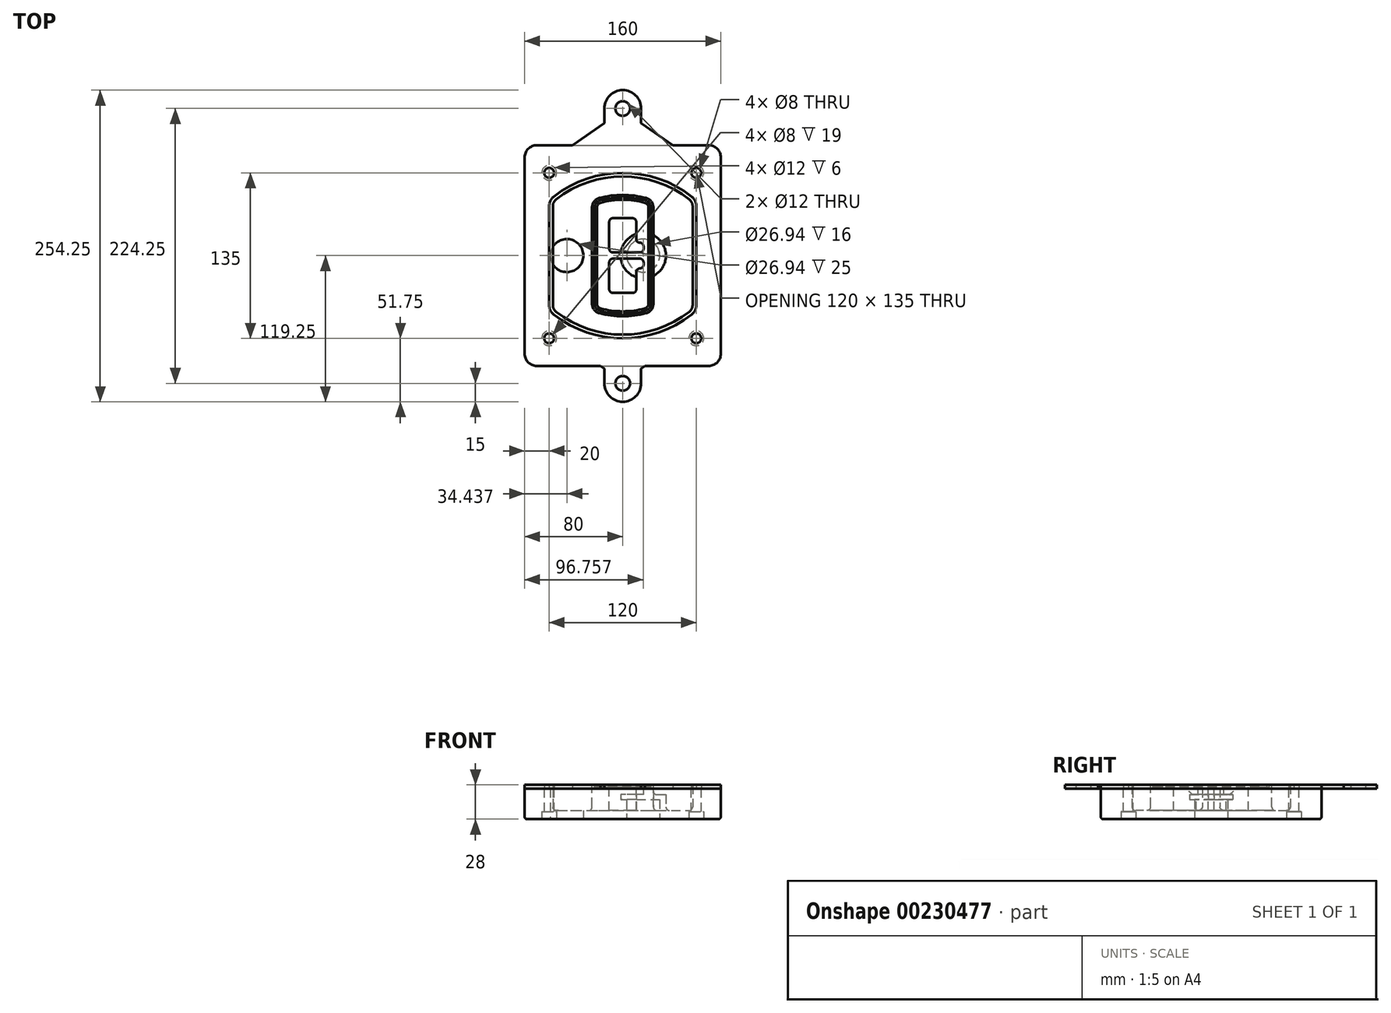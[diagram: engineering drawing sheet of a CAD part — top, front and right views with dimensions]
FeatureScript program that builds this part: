
annotation { "Feature Type Name" : "Feature", "Feature Type Description" : "" }
export const myFeature = defineFeature(function(context is Context, id is Id, definition is map)
    precondition{}
    {
        {
            var Q0;
            Q0=qCreatedBy(makeId("Top.planeOp"),FACE);
            var sketch = newSketch(context, id + "F0", { "sketchPlane" : qUnion([Q0])});
            skPoint(sketch, "E0.rect.middle", {"position": v(0, 0) * mm});
            skLineSegment(sketch, "E1.bottom", {"start": v(-70, -90) * mm, "end": v(70, -90) * mm});
            skLineSegment(sketch, "E1.top", {"start": v(-70, 90) * mm, "end": v(70, 90) * mm});
            skLineSegment(sketch, "E1.left", {"start": v(-80, -80) * mm, "end": v(-80, 80) * mm});
            skLineSegment(sketch, "E1.right", {"start": v(80, -80) * mm, "end": v(80, 80) * mm});
            skLineSegment(sketch, "E2", {"start": v(-80, 90) * mm, "end": v(80, -90) * mm, "construction": true});
            skLineSegment(sketch, "E3", {"start": v(80, 90) * mm, "end": v(-80, -90) * mm, "construction": true});
            skCircle(sketch, "E4", {"center": v(-60, 67.5) * mm, "radius": 4 * mm});
            skCircle(sketch, "E5", {"center": v(60, 67.5) * mm, "radius": 4 * mm});
            skCircle(sketch, "E6", {"center": v(60, -67.5) * mm, "radius": 4 * mm});
            skCircle(sketch, "E7", {"center": v(-60, -67.5) * mm, "radius": 4 * mm});
            skLineSegment(sketch, "E8", {"start": v(-60, 67.5) * mm, "end": v(60, 67.5) * mm, "construction": true});
            skLineSegment(sketch, "E9", {"start": v(60, 67.5) * mm, "end": v(60, -67.5) * mm, "construction": true});
            skLineSegment(sketch, "E10", {"start": v(60, -67.5) * mm, "end": v(-60, -67.5) * mm, "construction": true});
            skLineSegment(sketch, "E11", {"start": v(-60, -67.5) * mm, "end": v(-60, 67.5) * mm, "construction": true});
            skLineSegment(sketch, "E12", {"start": v(-60, 40.3) * mm, "end": v(-60, -40.3) * mm});
            skLineSegment(sketch, "E13", {"start": v(60, 40.3) * mm, "end": v(60, -40.3) * mm});
            skArc(sketch, "E14", {"start": v(56.15, 48.18) * mm, "mid": v(0, 67.5) * mm, "end": v(-56.15, 48.18) * mm});
            skArc(sketch, "E15", {"start": v(-56.15, -48.18) * mm, "mid": v(0, -67.5) * mm, "end": v(56.15, -48.18) * mm});
            skLineSegment(sketch, "E16", {"start": v(-60, 0) * mm, "end": v(60, 0) * mm, "construction": true});
            skPoint(sketch, "E17.visualSharp", {"position": v(-60, -45) * mm});
            skArc(sketch, "E17.filletArc", {"start": v(-60, -40.3) * mm, "mid": v(-58.99, -44.68) * mm, "end": v(-56.15, -48.18) * mm});
            skPoint(sketch, "E18.visualSharp", {"position": v(-60, 45) * mm});
            skArc(sketch, "E18.filletArc", {"start": v(-56.15, 48.18) * mm, "mid": v(-58.99, 44.68) * mm, "end": v(-60, 40.3) * mm});
            skPoint(sketch, "E19.visualSharp", {"position": v(60, 45) * mm});
            skArc(sketch, "E19.filletArc", {"start": v(60, 40.3) * mm, "mid": v(58.99, 44.68) * mm, "end": v(56.15, 48.18) * mm});
            skPoint(sketch, "E20.visualSharp", {"position": v(60, -45) * mm});
            skArc(sketch, "E20.filletArc", {"start": v(56.15, -48.18) * mm, "mid": v(58.99, -44.68) * mm, "end": v(60, -40.3) * mm});
            skPoint(sketch, "E21.visualSharp", {"position": v(-80, 90) * mm});
            skArc(sketch, "E21.filletArc", {"start": v(-70, 90) * mm, "mid": v(-77.07, 87.07) * mm, "end": v(-80, 80) * mm});
            skPoint(sketch, "E22.visualSharp", {"position": v(80, 90) * mm});
            skArc(sketch, "E22.filletArc", {"start": v(80, 80) * mm, "mid": v(77.07, 87.07) * mm, "end": v(70, 90) * mm});
            skPoint(sketch, "E23.visualSharp", {"position": v(80, -90) * mm});
            skArc(sketch, "E23.filletArc", {"start": v(70, -90) * mm, "mid": v(77.07, -87.07) * mm, "end": v(80, -80) * mm});
            skPoint(sketch, "E24.visualSharp", {"position": v(-80, -90) * mm});
            skArc(sketch, "E24.filletArc", {"start": v(-80, -80) * mm, "mid": v(-77.07, -87.07) * mm, "end": v(-70, -90) * mm});
            skArc(sketch, "E25.0", {"start": v(57, 40.3) * mm, "mid": v(56.3, 43.36) * mm, "end": v(54.3, 45.81) * mm});
            skLineSegment(sketch, "E25.1", {"start": v(57, 40.3) * mm, "end": v(57, -40.3) * mm});
            skArc(sketch, "E25.2", {"start": v(54.3, -45.81) * mm, "mid": v(56.3, -43.36) * mm, "end": v(57, -40.3) * mm});
            skArc(sketch, "E25.3", {"start": v(-54.3, -45.81) * mm, "mid": v(0, -64.5) * mm, "end": v(54.3, -45.81) * mm});
            skArc(sketch, "E25.4", {"start": v(-57, -40.3) * mm, "mid": v(-56.3, -43.36) * mm, "end": v(-54.3, -45.81) * mm});
            skArc(sketch, "E25.5", {"start": v(54.3, 45.81) * mm, "mid": v(0, 64.5) * mm, "end": v(-54.3, 45.81) * mm});
            skLineSegment(sketch, "E25.6", {"start": v(-57, 40.3) * mm, "end": v(-57, -40.3) * mm});
            skArc(sketch, "E25.7", {"start": v(-54.3, 45.81) * mm, "mid": v(-56.3, 43.36) * mm, "end": v(-57, 40.3) * mm});
            skArc(sketch, "E26.0", {"start": v(-58.62, 51.33) * mm, "mid": v(-62.58, 46.43) * mm, "end": v(-64, 40.3) * mm});
            skArc(sketch, "E26.1", {"start": v(58.62, 51.33) * mm, "mid": v(0, 71.5) * mm, "end": v(-58.62, 51.33) * mm});
            skArc(sketch, "E26.2", {"start": v(64, 40.3) * mm, "mid": v(62.58, 46.43) * mm, "end": v(58.62, 51.33) * mm});
            skLineSegment(sketch, "E26.3", {"start": v(64, 40.3) * mm, "end": v(64, -40.3) * mm});
            skArc(sketch, "E26.4", {"start": v(58.62, -51.33) * mm, "mid": v(62.58, -46.43) * mm, "end": v(64, -40.3) * mm});
            skLineSegment(sketch, "E26.5", {"start": v(-64, 40.3) * mm, "end": v(-64, -40.3) * mm});
            skArc(sketch, "E26.6", {"start": v(-58.62, -51.33) * mm, "mid": v(0, -71.5) * mm, "end": v(58.62, -51.33) * mm});
            skArc(sketch, "E26.7", {"start": v(-64, -40.3) * mm, "mid": v(-62.58, -46.43) * mm, "end": v(-58.62, -51.33) * mm});
            skSolve(sketch);
        }
        {
            var Q0;
            Q0=makeQuery(id+"F0.imprint","IMPRINT",FACE,{"disambiguationData":[TD([[makeQuery(id+"F0.imprint","IMPRINT",EDGE,{"derivedFrom":sQuery(id+"F0.wireOp",EDGE,"E1.bottom")}),1.0]])]});
            var Q1;
            Q1=makeQuery(id+"F0.imprint","IMPRINT",FACE,{"disambiguationData":[TD([[makeQuery(id+"F0.imprint","IMPRINT",EDGE,{"derivedFrom":sQuery(id+"F0.wireOp",EDGE,"E12")}),1.0]])]});
            var Q2;
            Q2=makeQuery(id+"F0.imprint","IMPRINT",FACE,{"disambiguationData":[TD([[makeQuery(id+"F0.imprint","IMPRINT",EDGE,{"derivedFrom":sQuery(id+"F0.wireOp",EDGE,"E25.0")}),1.0]])]});
            var Q3;
            Q3=makeQuery(id+"F0.imprint","IMPRINT",FACE,{"disambiguationData":[TD([[makeQuery(id+"F0.imprint","IMPRINT",EDGE,{"derivedFrom":sQuery(id+"F0.wireOp",EDGE,"E12")}),-1.0]])]});
            extrude(context, id + "F1", {"entities" : qUnion([Q0, Q1, Q2, Q3]), "oppositeDirection" : true, "depth" : 25 * mm});
        }
        {
            var Q0;
            Q0=makeQuery(id+"F0.imprint","IMPRINT",FACE,{"disambiguationData":[TD([[makeQuery(id+"F0.imprint","IMPRINT",EDGE,{"derivedFrom":sQuery(id+"F0.wireOp",EDGE,"E12")}),1.0]])]});
            extrude(context, id + "F2", {"entities" : qUnion([Q0]), "operationType" : NewBodyOperationType.ADD, "depth" : 3 * mm});
        }
        {
            var Q0;
            Q0=makeQuery(id+"F0.imprint","IMPRINT",FACE,{"disambiguationData":[TD([[makeQuery(id+"F0.imprint","IMPRINT",EDGE,{"derivedFrom":sQuery(id+"F0.wireOp",EDGE,"E25.0")}),1.0]])]});
            extrude(context, id + "F3", {"entities" : qUnion([Q0]), "operationType" : NewBodyOperationType.REMOVE, "oppositeDirection" : true, "depth" : 18 * mm});
        }
        {
            var Q0;
            Q0=makeQuery(id+"F2.opExtrude","CAP_FACE",FACE,{"disambiguationData":[OSD([sQuery(id+"F0.wireOp",EDGE,"E12"),sQuery(id+"F0.wireOp",EDGE,"E13"),sQuery(id+"F0.wireOp",EDGE,"E14"),sQuery(id+"F0.wireOp",EDGE,"E15"),sQuery(id+"F0.wireOp",EDGE,"E17.filletArc"),sQuery(id+"F0.wireOp",EDGE,"E18.filletArc"),sQuery(id+"F0.wireOp",EDGE,"E19.filletArc"),sQuery(id+"F0.wireOp",EDGE,"E20.filletArc"),sQuery(id+"F0.wireOp",EDGE,"E25.0"),sQuery(id+"F0.wireOp",EDGE,"E25.1"),sQuery(id+"F0.wireOp",EDGE,"E25.2"),sQuery(id+"F0.wireOp",EDGE,"E25.3"),sQuery(id+"F0.wireOp",EDGE,"E25.4"),sQuery(id+"F0.wireOp",EDGE,"E25.5"),sQuery(id+"F0.wireOp",EDGE,"E25.6"),sQuery(id+"F0.wireOp",EDGE,"E25.7")])],"isStart":false});
            var sketch = newSketch(context, id + "F4", { "sketchPlane" : qUnion([Q0])});
            skArc(sketch, "E27.0", {"start": v(-19.08, -46.97) * mm, "mid": v(0, -49.5) * mm, "end": v(19.08, -46.97) * mm});
            skArc(sketch, "E28.0", {"start": v(19.08, 46.97) * mm, "mid": v(0, 49.5) * mm, "end": v(-19.08, 46.97) * mm});
            skLineSegment(sketch, "E29", {"start": v(-25, 39.25) * mm, "end": v(-25, -39.25) * mm});
            skLineSegment(sketch, "E30", {"start": v(25, 39.25) * mm, "end": v(25, -39.25) * mm});
            skLineSegment(sketch, "E31", {"start": v(-25, 45.1) * mm, "end": v(25, 45.1) * mm, "construction": true});
            skLineSegment(sketch, "E32", {"start": v(-25, -45.1) * mm, "end": v(25, -45.1) * mm, "construction": true});
            skPoint(sketch, "E33.visualSharp", {"position": v(-25, 45.1) * mm});
            skArc(sketch, "E33.filletArc", {"start": v(-19.08, 46.97) * mm, "mid": v(-23.35, 44.11) * mm, "end": v(-25, 39.25) * mm});
            skPoint(sketch, "E34.visualSharp", {"position": v(25, 45.1) * mm});
            skArc(sketch, "E34.filletArc", {"start": v(25, 39.25) * mm, "mid": v(23.35, 44.11) * mm, "end": v(19.08, 46.97) * mm});
            skPoint(sketch, "E35.visualSharp", {"position": v(25, -45.1) * mm});
            skArc(sketch, "E35.filletArc", {"start": v(19.08, -46.97) * mm, "mid": v(23.35, -44.11) * mm, "end": v(25, -39.25) * mm});
            skPoint(sketch, "E36.visualSharp", {"position": v(-25, -45.1) * mm});
            skArc(sketch, "E36.filletArc", {"start": v(-25, -39.25) * mm, "mid": v(-23.35, -44.11) * mm, "end": v(-19.08, -46.97) * mm});
            skArc(sketch, "E37.0", {"start": v(54.3, 45.81) * mm, "mid": v(0, 64.5) * mm, "end": v(-54.3, 45.81) * mm});
            skArc(sketch, "E37.1", {"start": v(-54.3, 45.81) * mm, "mid": v(-56.3, 43.36) * mm, "end": v(-57, 40.3) * mm});
            skLineSegment(sketch, "E37.2", {"start": v(-57, 40.3) * mm, "end": v(-57, -40.3) * mm});
            skArc(sketch, "E37.3", {"start": v(-57, -40.3) * mm, "mid": v(-56.3, -43.36) * mm, "end": v(-54.3, -45.81) * mm});
            skArc(sketch, "E37.4", {"start": v(-54.3, -45.81) * mm, "mid": v(0, -64.5) * mm, "end": v(54.3, -45.81) * mm});
            skArc(sketch, "E37.5", {"start": v(54.3, -45.81) * mm, "mid": v(56.3, -43.36) * mm, "end": v(57, -40.3) * mm});
            skLineSegment(sketch, "E37.6", {"start": v(57, 40.3) * mm, "end": v(57, -40.3) * mm});
            skArc(sketch, "E37.7", {"start": v(57, 40.3) * mm, "mid": v(56.3, 43.36) * mm, "end": v(54.3, 45.81) * mm});
            skLineSegment(sketch, "E38.0", {"start": v(23, 39.25) * mm, "end": v(23, -39.25) * mm});
            skArc(sketch, "E38.1", {"start": v(18.56, -45.04) * mm, "mid": v(21.76, -42.9) * mm, "end": v(23, -39.25) * mm});
            skArc(sketch, "E38.2", {"start": v(-18.56, -45.04) * mm, "mid": v(0, -47.5) * mm, "end": v(18.56, -45.04) * mm});
            skArc(sketch, "E38.3", {"start": v(-23, -39.25) * mm, "mid": v(-21.76, -42.9) * mm, "end": v(-18.56, -45.04) * mm});
            skLineSegment(sketch, "E38.4", {"start": v(-23, 39.25) * mm, "end": v(-23, -39.25) * mm});
            skArc(sketch, "E38.5", {"start": v(23, 39.25) * mm, "mid": v(21.76, 42.9) * mm, "end": v(18.56, 45.04) * mm});
            skArc(sketch, "E38.6", {"start": v(-18.56, 45.04) * mm, "mid": v(-21.76, 42.9) * mm, "end": v(-23, 39.25) * mm});
            skArc(sketch, "E38.7", {"start": v(18.56, 45.04) * mm, "mid": v(0, 47.5) * mm, "end": v(-18.56, 45.04) * mm});
            skArc(sketch, "E39.0", {"start": v(21, 39.25) * mm, "mid": v(20.18, 41.68) * mm, "end": v(18.04, 43.1) * mm});
            skLineSegment(sketch, "E39.1", {"start": v(21, 39.25) * mm, "end": v(21, -39.25) * mm});
            skArc(sketch, "E39.2", {"start": v(18.04, -43.1) * mm, "mid": v(20.18, -41.68) * mm, "end": v(21, -39.25) * mm});
            skArc(sketch, "E39.3", {"start": v(-18.04, -43.1) * mm, "mid": v(0, -45.5) * mm, "end": v(18.04, -43.1) * mm});
            skArc(sketch, "E39.4", {"start": v(-21, -39.25) * mm, "mid": v(-20.18, -41.68) * mm, "end": v(-18.04, -43.1) * mm});
            skArc(sketch, "E39.5", {"start": v(18.04, 43.1) * mm, "mid": v(0, 45.5) * mm, "end": v(-18.04, 43.1) * mm});
            skLineSegment(sketch, "E39.6", {"start": v(-21, 39.25) * mm, "end": v(-21, -39.25) * mm});
            skArc(sketch, "E39.7", {"start": v(-18.04, 43.1) * mm, "mid": v(-20.18, 41.68) * mm, "end": v(-21, 39.25) * mm});
            skLineSegment(sketch, "E40", {"start": v(-25, 0) * mm, "end": v(25, 0) * mm, "construction": true});
            skLineSegment(sketch, "E41", {"start": v(-11, 5.5) * mm, "end": v(-11, 27.5) * mm});
            skLineSegment(sketch, "E42", {"start": v(-8, 30.5) * mm, "end": v(8, 30.5) * mm});
            skLineSegment(sketch, "E43", {"start": v(11, 27.5) * mm, "end": v(11, 13.5) * mm});
            skLineSegment(sketch, "E44", {"start": v(14, 10.5) * mm, "end": v(14, 10.5) * mm});
            skLineSegment(sketch, "E45", {"start": v(17, 7.5) * mm, "end": v(17, 5.5) * mm});
            skLineSegment(sketch, "E46", {"start": v(14, 2.5) * mm, "end": v(-8, 2.5) * mm});
            skPoint(sketch, "E47.visualSharp", {"position": v(-11, 30.5) * mm});
            skArc(sketch, "E47.filletArc", {"start": v(-8, 30.5) * mm, "mid": v(-10.12, 29.62) * mm, "end": v(-11, 27.5) * mm});
            skPoint(sketch, "E48.visualSharp", {"position": v(11, 30.5) * mm});
            skArc(sketch, "E48.filletArc", {"start": v(11, 27.5) * mm, "mid": v(10.12, 29.62) * mm, "end": v(8, 30.5) * mm});
            skPoint(sketch, "E49.visualSharp", {"position": v(11, 10.5) * mm});
            skArc(sketch, "E49.filletArc", {"start": v(11, 13.5) * mm, "mid": v(11.88, 11.38) * mm, "end": v(14, 10.5) * mm});
            skPoint(sketch, "E50.visualSharp", {"position": v(17, 10.5) * mm});
            skArc(sketch, "E50.filletArc", {"start": v(17, 7.5) * mm, "mid": v(16.12, 9.62) * mm, "end": v(14, 10.5) * mm});
            skPoint(sketch, "E51.visualSharp", {"position": v(17, 2.5) * mm});
            skArc(sketch, "E51.filletArc", {"start": v(14, 2.5) * mm, "mid": v(16.12, 3.38) * mm, "end": v(17, 5.5) * mm});
            skPoint(sketch, "E52.visualSharp", {"position": v(-11, 2.5) * mm});
            skArc(sketch, "E52.filletArc", {"start": v(-11, 5.5) * mm, "mid": v(-10.12, 3.38) * mm, "end": v(-8, 2.5) * mm});
            skLineSegment(sketch, "E53.0.MirrorCS", {"start": v(14, -2.5) * mm, "end": v(-8, -2.5) * mm});
            skArc(sketch, "E54.0.MirrorCS", {"start": v(-11, -5.5) * mm, "mid": v(-10.12, -3.38) * mm, "end": v(-8, -2.5) * mm});
            skLineSegment(sketch, "E55.0.MirrorCS", {"start": v(-11, -5.5) * mm, "end": v(-11, -27.5) * mm});
            skArc(sketch, "E56.0.MirrorCS", {"start": v(-8, -30.5) * mm, "mid": v(-10.12, -29.62) * mm, "end": v(-11, -27.5) * mm});
            skLineSegment(sketch, "E57.0.MirrorCS", {"start": v(-8, -30.5) * mm, "end": v(8, -30.5) * mm});
            skArc(sketch, "E58.0.MirrorCS", {"start": v(11, -27.5) * mm, "mid": v(10.12, -29.62) * mm, "end": v(8, -30.5) * mm});
            skLineSegment(sketch, "E59.0.MirrorCS", {"start": v(11, -27.5) * mm, "end": v(11, -13.5) * mm});
            skArc(sketch, "E60.0.MirrorCS", {"start": v(11, -13.5) * mm, "mid": v(11.88, -11.38) * mm, "end": v(14, -10.5) * mm});
            skArc(sketch, "E61.0.MirrorCS", {"start": v(17, -7.5) * mm, "mid": v(16.12, -9.62) * mm, "end": v(14, -10.5) * mm});
            skLineSegment(sketch, "E62.0.MirrorCS", {"start": v(17, -7.5) * mm, "end": v(17, -5.5) * mm});
            skArc(sketch, "E63.0.MirrorCS", {"start": v(14, -2.5) * mm, "mid": v(16.12, -3.38) * mm, "end": v(17, -5.5) * mm});
            skSolve(sketch);
        }
        {
            var Q0;
            Q0=makeQuery(id+"F4.imprint","IMPRINT",FACE,{"disambiguationData":[TD([[makeQuery(id+"F4.imprint","IMPRINT",EDGE,{"derivedFrom":sQuery(id+"F4.wireOp",EDGE,"E27.0")}),1.0]])]});
            var Q1;
            Q1=makeQuery(id+"F4.imprint","IMPRINT",FACE,{"disambiguationData":[TD([[makeQuery(id+"F4.imprint","IMPRINT",EDGE,{"derivedFrom":sQuery(id+"F4.wireOp",EDGE,"E38.0")}),-1.0]])]});
            var Q2;
            Q2=makeQuery(id+"F4.imprint","IMPRINT",FACE,{"disambiguationData":[TD([[makeQuery(id+"F4.imprint","IMPRINT",EDGE,{"derivedFrom":sQuery(id+"F4.wireOp",EDGE,"E39.0")}),1.0]])]});
            extrude(context, id + "F5", {"entities" : qUnion([Q0, Q1, Q2]), "operationType" : NewBodyOperationType.ADD, "endBound" : BoundingType.UP_TO_NEXT, "oppositeDirection" : true, "depth" : 25 * mm});
        }
        {
            var Q0;
            Q0=makeQuery(id+"F4.imprint","IMPRINT",FACE,{"disambiguationData":[TD([[makeQuery(id+"F4.imprint","IMPRINT",EDGE,{"derivedFrom":sQuery(id+"F4.wireOp",EDGE,"E38.0")}),-1.0]])]});
            extrude(context, id + "F6", {"entities" : qUnion([Q0]), "operationType" : NewBodyOperationType.REMOVE, "oppositeDirection" : true, "depth" : 2 * mm});
        }
        {
            var Q0;
            Q0=makeQuery(id+"F1.opExtrude","CAP_FACE",FACE,{"disambiguationData":[OSD([sQuery(id+"F0.wireOp",EDGE,"E1.bottom"),sQuery(id+"F0.wireOp",EDGE,"E1.top"),sQuery(id+"F0.wireOp",EDGE,"E1.left"),sQuery(id+"F0.wireOp",EDGE,"E1.right"),sQuery(id+"F0.wireOp",EDGE,"E4"),sQuery(id+"F0.wireOp",EDGE,"E5"),sQuery(id+"F0.wireOp",EDGE,"E6"),sQuery(id+"F0.wireOp",EDGE,"E7"),sQuery(id+"F0.wireOp",EDGE,"E21.filletArc"),sQuery(id+"F0.wireOp",EDGE,"E22.filletArc"),sQuery(id+"F0.wireOp",EDGE,"E23.filletArc"),sQuery(id+"F0.wireOp",EDGE,"E24.filletArc")])],"isStart":false});
            var sketch = newSketch(context, id + "F7", { "sketchPlane" : qUnion([Q0])});
            skCircle(sketch, "E64", {"center": v(16.76, 0) * mm, "radius": 13.47 * mm});
            skCircle(sketch, "E65", {"center": v(-45.56, 0) * mm, "radius": 13.47 * mm});
            skLineSegment(sketch, "E66", {"start": v(80, 0) * mm, "end": v(-80, 0) * mm});
            skCircle(sketch, "E67", {"center": v(16.76, 0) * mm, "radius": 18.47 * mm});
            skCircle(sketch, "E68", {"center": v(60, -67.5) * mm, "radius": 6 * mm});
            skCircle(sketch, "E69", {"center": v(-60, -67.5) * mm, "radius": 6 * mm});
            skCircle(sketch, "E70", {"center": v(-60, 67.5) * mm, "radius": 6 * mm});
            skCircle(sketch, "E71", {"center": v(60, 67.5) * mm, "radius": 6 * mm});
            skSolve(sketch);
        }
        {
            var Q0;
            {var subQ1=sQuery(id+"F7.wireOp",EDGE,"E66");var subQ4=sQuery(id+"F7.wireOp",EDGE,"E64");var subQ6=makeQuery(id+"F7.imprint","INTERSECT",VERTEX,{"disambiguationData":[OD(0.0)],"derivedFrom":[subQ4,subQ1]});Q0=makeQuery(id+"F7.imprint","IMPRINT",FACE,{"disambiguationData":[TD([[makeQuery(id+"F7.imprint","IMPRINT",EDGE,{"disambiguationData":[TD([[subQ6,-1.0]])],"derivedFrom":subQ4}),-1.0]])]});}
            var Q1;
            {var subQ0=sQuery(id+"F7.wireOp",EDGE,"E66");var subQ1=sQuery(id+"F7.wireOp",EDGE,"E64");var subQ3=makeQuery(id+"F7.imprint","INTERSECT",VERTEX,{"disambiguationData":[OD(0.0)],"derivedFrom":[subQ1,subQ0]});Q1=makeQuery(id+"F7.imprint","IMPRINT",FACE,{"disambiguationData":[TD([[makeQuery(id+"F7.imprint","IMPRINT",EDGE,{"disambiguationData":[TD([[subQ3,-1.0]])],"derivedFrom":subQ1}),1.0]])]});}
            var Q2;
            {var subQ0=sQuery(id+"F7.wireOp",EDGE,"E66");var subQ1=sQuery(id+"F7.wireOp",EDGE,"E64");var subQ3=makeQuery(id+"F7.imprint","INTERSECT",VERTEX,{"disambiguationData":[OD(0.0)],"derivedFrom":[subQ1,subQ0]});Q2=makeQuery(id+"F7.imprint","IMPRINT",FACE,{"disambiguationData":[TD([[makeQuery(id+"F7.imprint","IMPRINT",EDGE,{"disambiguationData":[TD([[subQ3,1.0]])],"derivedFrom":subQ1}),1.0]])]});}
            var Q3;
            {var subQ1=sQuery(id+"F7.wireOp",EDGE,"E66");var subQ4=sQuery(id+"F7.wireOp",EDGE,"E64");var subQ6=makeQuery(id+"F7.imprint","INTERSECT",VERTEX,{"disambiguationData":[OD(0.0)],"derivedFrom":[subQ4,subQ1]});Q3=makeQuery(id+"F7.imprint","IMPRINT",FACE,{"disambiguationData":[TD([[makeQuery(id+"F7.imprint","IMPRINT",EDGE,{"disambiguationData":[TD([[subQ6,1.0]])],"derivedFrom":subQ4}),-1.0]])]});}
            extrude(context, id + "F8", {"entities" : qUnion([Q0, Q1, Q2, Q3]), "operationType" : NewBodyOperationType.ADD, "oppositeDirection" : true, "depth" : 20 * mm});
        }
        {
            var Q0;
            {var subQ0=sQuery(id+"F7.wireOp",EDGE,"E66");var subQ1=sQuery(id+"F7.wireOp",EDGE,"E64");var subQ3=makeQuery(id+"F7.imprint","INTERSECT",VERTEX,{"disambiguationData":[OD(0.0)],"derivedFrom":[subQ1,subQ0]});Q0=makeQuery(id+"F7.imprint","IMPRINT",FACE,{"disambiguationData":[TD([[makeQuery(id+"F7.imprint","IMPRINT",EDGE,{"disambiguationData":[TD([[subQ3,-1.0]])],"derivedFrom":subQ1}),1.0]])]});}
            var Q1;
            {var subQ0=sQuery(id+"F7.wireOp",EDGE,"E66");var subQ1=sQuery(id+"F7.wireOp",EDGE,"E64");var subQ3=makeQuery(id+"F7.imprint","INTERSECT",VERTEX,{"disambiguationData":[OD(0.0)],"derivedFrom":[subQ1,subQ0]});Q1=makeQuery(id+"F7.imprint","IMPRINT",FACE,{"disambiguationData":[TD([[makeQuery(id+"F7.imprint","IMPRINT",EDGE,{"disambiguationData":[TD([[subQ3,1.0]])],"derivedFrom":subQ1}),1.0]])]});}
            extrude(context, id + "F9", {"entities" : qUnion([Q0, Q1]), "operationType" : NewBodyOperationType.REMOVE, "oppositeDirection" : true, "depth" : 16 * mm});
        }
        {
            var Q0;
            {var subQ0=sQuery(id+"F7.wireOp",EDGE,"E66");var subQ1=sQuery(id+"F7.wireOp",EDGE,"E65");var subQ3=makeQuery(id+"F7.imprint","INTERSECT",VERTEX,{"disambiguationData":[OD(0.0)],"derivedFrom":[subQ1,subQ0]});Q0=makeQuery(id+"F7.imprint","IMPRINT",FACE,{"disambiguationData":[TD([[makeQuery(id+"F7.imprint","IMPRINT",EDGE,{"disambiguationData":[TD([[subQ3,-1.0]])],"derivedFrom":subQ1}),1.0]])]});}
            var Q1;
            {var subQ0=sQuery(id+"F7.wireOp",EDGE,"E66");var subQ1=sQuery(id+"F7.wireOp",EDGE,"E65");var subQ3=makeQuery(id+"F7.imprint","INTERSECT",VERTEX,{"disambiguationData":[OD(0.0)],"derivedFrom":[subQ1,subQ0]});Q1=makeQuery(id+"F7.imprint","IMPRINT",FACE,{"disambiguationData":[TD([[makeQuery(id+"F7.imprint","IMPRINT",EDGE,{"disambiguationData":[TD([[subQ3,1.0]])],"derivedFrom":subQ1}),1.0]])]});}
            extrude(context, id + "F10", {"entities" : qUnion([Q0, Q1]), "operationType" : NewBodyOperationType.REMOVE, "oppositeDirection" : true, "depth" : 25 * mm});
        }
        {
            var Q0;
            Q0=makeQuery(id+"F7.imprint","IMPRINT",FACE,{"disambiguationData":[TD([[makeQuery(id+"F7.imprint","IMPRINT",EDGE,{"derivedFrom":sQuery(id+"F7.wireOp",EDGE,"E68")}),1.0]])]});
            var Q1;
            Q1=makeQuery(id+"F7.imprint","IMPRINT",FACE,{"disambiguationData":[TD([[makeQuery(id+"F7.imprint","IMPRINT",EDGE,{"derivedFrom":makeQuery(id+"F1.opExtrude","CAP_EDGE",EDGE,{"disambiguationData":[OSD([sQuery(id+"F0.wireOp",EDGE,"E5")])],"isStart":false})}),-1.0]])]});
            var Q2;
            Q2=makeQuery(id+"F7.imprint","IMPRINT",FACE,{"disambiguationData":[TD([[makeQuery(id+"F7.imprint","IMPRINT",EDGE,{"derivedFrom":sQuery(id+"F7.wireOp",EDGE,"E69")}),1.0]])]});
            var Q3;
            Q3=makeQuery(id+"F7.imprint","IMPRINT",FACE,{"disambiguationData":[TD([[makeQuery(id+"F7.imprint","IMPRINT",EDGE,{"derivedFrom":makeQuery(id+"F1.opExtrude","CAP_EDGE",EDGE,{"disambiguationData":[OSD([sQuery(id+"F0.wireOp",EDGE,"E4")])],"isStart":false})}),-1.0]])]});
            var Q4;
            Q4=makeQuery(id+"F7.imprint","IMPRINT",FACE,{"disambiguationData":[TD([[makeQuery(id+"F7.imprint","IMPRINT",EDGE,{"derivedFrom":sQuery(id+"F7.wireOp",EDGE,"E70")}),1.0]])]});
            var Q5;
            Q5=makeQuery(id+"F7.imprint","IMPRINT",FACE,{"disambiguationData":[TD([[makeQuery(id+"F7.imprint","IMPRINT",EDGE,{"derivedFrom":makeQuery(id+"F1.opExtrude","CAP_EDGE",EDGE,{"disambiguationData":[OSD([sQuery(id+"F0.wireOp",EDGE,"E7")])],"isStart":false})}),-1.0]])]});
            var Q6;
            Q6=makeQuery(id+"F7.imprint","IMPRINT",FACE,{"disambiguationData":[TD([[makeQuery(id+"F7.imprint","IMPRINT",EDGE,{"derivedFrom":sQuery(id+"F7.wireOp",EDGE,"E71")}),1.0]])]});
            var Q7;
            Q7=makeQuery(id+"F7.imprint","IMPRINT",FACE,{"disambiguationData":[TD([[makeQuery(id+"F7.imprint","IMPRINT",EDGE,{"derivedFrom":makeQuery(id+"F1.opExtrude","CAP_EDGE",EDGE,{"disambiguationData":[OSD([sQuery(id+"F0.wireOp",EDGE,"E6")])],"isStart":false})}),-1.0]])]});
            extrude(context, id + "F11", {"entities" : qUnion([Q0, Q1, Q2, Q3, Q4, Q5, Q6, Q7]), "operationType" : NewBodyOperationType.REMOVE, "oppositeDirection" : true, "depth" : 6 * mm});
        }
        {
            var Q0;
            Q0=makeQuery(id+"F9.boolean.opBoolean","COPY",FACE,{"derivedFrom":makeQuery(id+"F9.opExtrude","CAP_FACE",FACE,{"disambiguationData":[OSD([sQuery(id+"F7.wireOp",EDGE,"E64")])],"isStart":false})});
            var sketch = newSketch(context, id + "F12", { "sketchPlane" : qUnion([Q0])});
            skArc(sketch, "E72.0", {"start": v(11, 17.55) * mm, "mid": v(2.57, 11.82) * mm, "end": v(-1.54, 2.5) * mm});
            skArc(sketch, "E72.1", {"start": v(-1.54, -2.5) * mm, "mid": v(2.57, -11.82) * mm, "end": v(11, -17.55) * mm});
            skLineSegment(sketch, "E73", {"start": v(-1.54, -2.5) * mm, "end": v(14, -2.5) * mm});
            skLineSegment(sketch, "E74.0", {"start": v(14, 2.5) * mm, "end": v(-1.54, 2.5) * mm});
            skArc(sketch, "E74.1", {"start": v(14, 2.5) * mm, "mid": v(16.12, 3.38) * mm, "end": v(17, 5.5) * mm});
            skLineSegment(sketch, "E74.2", {"start": v(17, 7.5) * mm, "end": v(17, 5.5) * mm});
            skArc(sketch, "E74.3", {"start": v(17, 7.5) * mm, "mid": v(16.12, 9.62) * mm, "end": v(14, 10.5) * mm});
            skArc(sketch, "E74.4", {"start": v(11, 13.5) * mm, "mid": v(11.88, 11.38) * mm, "end": v(14, 10.5) * mm});
            skLineSegment(sketch, "E74.5", {"start": v(11, 17.55) * mm, "end": v(11, 13.5) * mm});
            skLineSegment(sketch, "E74.7", {"start": v(14, -2.5) * mm, "end": v(-1.54, -2.5) * mm});
            skArc(sketch, "E74.8", {"start": v(14, -2.5) * mm, "mid": v(16.12, -3.38) * mm, "end": v(17, -5.5) * mm});
            skLineSegment(sketch, "E74.9", {"start": v(17, -7.5) * mm, "end": v(17, -5.5) * mm});
            skArc(sketch, "E74.10", {"start": v(17, -7.5) * mm, "mid": v(16.12, -9.62) * mm, "end": v(14, -10.5) * mm});
            skArc(sketch, "E74.11", {"start": v(11, -13.5) * mm, "mid": v(11.88, -11.38) * mm, "end": v(14, -10.5) * mm});
            skLineSegment(sketch, "E74.12", {"start": v(11, -17.55) * mm, "end": v(11, -13.5) * mm});
            skPoint(sketch, "E75.orphan", {"position": v(11, -27.5) * mm});
            skPoint(sketch, "E76.orphan", {"position": v(-8, -2.5) * mm});
            skPoint(sketch, "E77.orphan", {"position": v(-8, 2.5) * mm});
            skPoint(sketch, "E78.orphan", {"position": v(11, 27.5) * mm});
            skSolve(sketch);
        }
        {
            var Q0;
            {var subQ7=sQuery(id+"F12.wireOp",EDGE,"E72.0");var subQ14=sQuery(id+"F12.wireOp",EDGE,"E72.1");var subQ16=sQuery(id+"F12.wireOp",EDGE,"E74.1");var subQ18=sQuery(id+"F12.wireOp",EDGE,"E74.8");Q0=qUnion([makeQuery(id+"F12.imprint","IMPRINT",FACE,{"disambiguationData":[TD([[makeQuery(id+"F12.imprint","IMPRINT",EDGE,{"derivedFrom":subQ7}),1.0]])]}),makeQuery(id+"F12.imprint","IMPRINT",FACE,{"disambiguationData":[TD([[makeQuery(id+"F12.imprint","IMPRINT",EDGE,{"derivedFrom":subQ14}),1.0]])]}),makeQuery(id+"F12.imprint","IMPRINT",FACE,{"disambiguationData":[TD([[makeQuery(id+"F12.imprint","IMPRINT",EDGE,{"derivedFrom":subQ16}),1.0]])]}),makeQuery(id+"F12.imprint","IMPRINT",FACE,{"disambiguationData":[TD([[makeQuery(id+"F12.imprint","IMPRINT",EDGE,{"derivedFrom":subQ18}),-1.0]])]})]);}
            var Q1;
            Q1=makeQuery(id+"F5.boolean.opBoolean","SPLIT",FACE,{"disambiguationData":[TD([makeQuery(id+"F5.opExtrude","SWEPT_FACE",FACE,{"disambiguationData":[OSD([sQuery(id+"F4.wireOp",EDGE,"E41")])]})])],"derivedFrom":makeQuery(id+"F3.boolean.opBoolean","COPY",FACE,{"derivedFrom":makeQuery(id+"F3.opExtrude","CAP_FACE",FACE,{"disambiguationData":[OSD([sQuery(id+"F0.wireOp",EDGE,"E25.0"),sQuery(id+"F0.wireOp",EDGE,"E25.1"),sQuery(id+"F0.wireOp",EDGE,"E25.2"),sQuery(id+"F0.wireOp",EDGE,"E25.3"),sQuery(id+"F0.wireOp",EDGE,"E25.4"),sQuery(id+"F0.wireOp",EDGE,"E25.5"),sQuery(id+"F0.wireOp",EDGE,"E25.6"),sQuery(id+"F0.wireOp",EDGE,"E25.7")])],"isStart":false})})});
            extrude(context, id + "F13", {"entities" : qUnion([Q0]), "operationType" : NewBodyOperationType.REMOVE, "endBound" : BoundingType.UP_TO_SURFACE, "endBoundEntityFace" : qUnion([Q1]), "depth" : 25 * mm});
        }
        {
            var Q0;
            Q0=makeQuery(id+"F3.boolean.opBoolean","COPY",EDGE,{"derivedFrom":makeQuery(id+"F3.opExtrude","CAP_EDGE",EDGE,{"disambiguationData":[OSD([sQuery(id+"F0.wireOp",EDGE,"E25.6")])],"isStart":false})});
            var Q1;
            Q1=makeQuery(id+"F8.boolean.opBoolean","INTERSECT",EDGE,{"derivedFrom":[makeQuery(id+"F5.opExtrude","SWEPT_FACE",FACE,{"disambiguationData":[OSD([sQuery(id+"F4.wireOp",EDGE,"E30")])]}),makeQuery(id+"F8.opExtrude","CAP_FACE",FACE,{"disambiguationData":[OSD([sQuery(id+"F7.wireOp",EDGE,"E67")])],"isStart":false})]});
            var Q2;
            Q2=makeQuery(id+"F8.boolean.opBoolean","INTERSECT",EDGE,{"disambiguationData":[OD(1.0)],"derivedFrom":[makeQuery(id+"F5.opExtrude","SWEPT_FACE",FACE,{"disambiguationData":[OSD([sQuery(id+"F4.wireOp",EDGE,"E30")])]}),makeQuery(id+"F8.opExtrude","SWEPT_FACE",FACE,{"disambiguationData":[OSD([sQuery(id+"F7.wireOp",EDGE,"E67")])]})]});
            var Q3;
            {var subQ0=sQuery(id+"F4.wireOp",EDGE,"E30");Q3=makeQuery(id+"F8.boolean.opBoolean","SPLIT",EDGE,{"disambiguationData":[TD([makeQuery(id+"F5.opExtrude","SWEPT_FACE",FACE,{"disambiguationData":[OSD([sQuery(id+"F4.wireOp",EDGE,"E35.filletArc")])]})])],"derivedFrom":makeQuery(id+"F5.opExtrude","CAP_EDGE",EDGE,{"disambiguationData":[OSD([subQ0])],"isStart":false})});}
            var Q4;
            {var subQ0=sQuery(id+"F0.wireOp",EDGE,"E25.7");var subQ1=sQuery(id+"F0.wireOp",EDGE,"E25.1");var subQ2=sQuery(id+"F0.wireOp",EDGE,"E25.6");var subQ3=sQuery(id+"F0.wireOp",EDGE,"E25.5");var subQ4=sQuery(id+"F0.wireOp",EDGE,"E25.4");var subQ5=sQuery(id+"F0.wireOp",EDGE,"E25.0");var subQ6=sQuery(id+"F0.wireOp",EDGE,"E25.2");var subQ7=sQuery(id+"F0.wireOp",EDGE,"E25.3");Q4=makeQuery(id+"F8.boolean.opBoolean","INTERSECT",EDGE,{"derivedFrom":[makeQuery(id+"F5.boolean.opBoolean","SPLIT",FACE,{"disambiguationData":[TD([makeQuery(id+"F2.opExtrude","SWEPT_FACE",FACE,{"disambiguationData":[OSD([subQ5])]})])],"derivedFrom":makeQuery(id+"F3.boolean.opBoolean","COPY",FACE,{"derivedFrom":makeQuery(id+"F3.opExtrude","CAP_FACE",FACE,{"disambiguationData":[OSD([subQ5,subQ1,subQ6,subQ7,subQ4,subQ3,subQ2,subQ0])],"isStart":false})})}),makeQuery(id+"F8.opExtrude","SWEPT_FACE",FACE,{"disambiguationData":[OSD([sQuery(id+"F7.wireOp",EDGE,"E67")])]})]});}
            var Q5;
            Q5=makeQuery(id+"F8.boolean.opBoolean","INTERSECT",EDGE,{"disambiguationData":[OD(0.0)],"derivedFrom":[makeQuery(id+"F5.opExtrude","SWEPT_FACE",FACE,{"disambiguationData":[OSD([sQuery(id+"F4.wireOp",EDGE,"E30")])]}),makeQuery(id+"F8.opExtrude","SWEPT_FACE",FACE,{"disambiguationData":[OSD([sQuery(id+"F7.wireOp",EDGE,"E67")])]})]});
            fillet(context, id + "F14", {"entities" : qUnion([Q0, Q1, Q2, Q3, Q4, Q5]), "radius" : 3 * mm, "tangentPropagation" : true, "allowEdgeOverflow" : false});
        }
        {
            var Q0;
            Q0=makeQuery(id+"F1.opExtrude","CAP_EDGE",EDGE,{"disambiguationData":[OSD([sQuery(id+"F0.wireOp",EDGE,"E1.bottom")])],"isStart":false});
            fillet(context, id + "F15", {"entities" : qUnion([Q0]), "radius" : 2 * mm, "tangentPropagation" : true, "allowEdgeOverflow" : false});
        }
        {
            var Q0;
            {var subQ0=sQuery(id+"F0.wireOp",EDGE,"E22.filletArc");var subQ1=sQuery(id+"F0.wireOp",EDGE,"E7");var subQ2=sQuery(id+"F0.wireOp",EDGE,"E6");var subQ3=sQuery(id+"F0.wireOp",EDGE,"E5");var subQ4=sQuery(id+"F0.wireOp",EDGE,"E4");var subQ5=sQuery(id+"F0.wireOp",EDGE,"E1.bottom");var subQ6=sQuery(id+"F0.wireOp",EDGE,"E21.filletArc");var subQ7=sQuery(id+"F0.wireOp",EDGE,"E1.top");var subQ8=sQuery(id+"F0.wireOp",EDGE,"E1.left");var subQ9=sQuery(id+"F0.wireOp",EDGE,"E1.right");var subQ10=sQuery(id+"F0.wireOp",EDGE,"E23.filletArc");var subQ11=sQuery(id+"F0.wireOp",EDGE,"E24.filletArc");Q0=makeQuery(id+"F2.boolean.opBoolean","SPLIT",FACE,{"disambiguationData":[TD([makeQuery(id+"F1.opExtrude","SWEPT_FACE",FACE,{"disambiguationData":[OSD([subQ5])]})])],"derivedFrom":makeQuery(id+"F1.opExtrude","CAP_FACE",FACE,{"disambiguationData":[OSD([subQ5,subQ7,subQ8,subQ9,subQ4,subQ3,subQ2,subQ1,subQ6,subQ0,subQ10,subQ11])],"isStart":true})});}
            var sketch = newSketch(context, id + "F16", { "sketchPlane" : qUnion([Q0])});
            skLineSegment(sketch, "E79", {"start": v(0, 90) * mm, "end": v(0, 120) * mm});
            skCircle(sketch, "E80", {"center": v(0, 120) * mm, "radius": 6 * mm});
            skArc(sketch, "E81", {"start": v(15, 120) * mm, "mid": v(0, 135) * mm, "end": v(-15, 120) * mm});
            skLineSegment(sketch, "E82", {"start": v(-40.9, 90) * mm, "end": v(-14.94, 108) * mm});
            skLineSegment(sketch, "E83", {"start": v(-15, 120) * mm, "end": v(-14.94, 108) * mm});
            skLineSegment(sketch, "E84.MirrorCS", {"start": v(15, 120) * mm, "end": v(14.94, 108) * mm});
            skLineSegment(sketch, "E85.MirrorCS", {"start": v(40.9, 90) * mm, "end": v(14.94, 108) * mm});
            skPoint(sketch, "E86.endSnap0", {"position": v(-60, 0) * mm});
            skPoint(sketch, "E87.endSnap0", {"position": v(80, 0) * mm});
            skLineSegment(sketch, "E88.MirrorCS", {"start": v(15, -104.25) * mm, "end": v(14.94, -92.25) * mm});
            skLineSegment(sketch, "E89.MirrorCS", {"start": v(40.9, -74.25) * mm, "end": v(14.94, -92.25) * mm});
            skArc(sketch, "E90.MirrorCS", {"start": v(15, -104.25) * mm, "mid": v(0, -119.25) * mm, "end": v(-15, -104.25) * mm});
            skLineSegment(sketch, "E91.MirrorCS", {"start": v(-40.9, -74.25) * mm, "end": v(-14.94, -92.25) * mm});
            skCircle(sketch, "E92.MirrorC", {"center": v(0, -104.25) * mm, "radius": 6 * mm});
            skLineSegment(sketch, "E93.MirrorCS", {"start": v(-15, -104.25) * mm, "end": v(-14.94, -92.25) * mm});
            skLineSegment(sketch, "E94.MirrorCS", {"start": v(0, -74.25) * mm, "end": v(0, -104.25) * mm});
            skSolve(sketch);
        }
        {
            var Q0;
            Q0=makeQuery(id+"F16.imprint","IMPRINT",FACE,{"disambiguationData":[TD([[makeQuery(id+"F16.imprint","IMPRINT",EDGE,{"derivedFrom":makeQuery(id+"F1.opExtrude","CAP_EDGE",EDGE,{"disambiguationData":[OSD([sQuery(id+"F0.wireOp",EDGE,"E1.left")])],"isStart":true})}),-1.0]])]});
            var Q1;
            Q1=makeQuery(id+"F16.imprint","IMPRINT",FACE,{"disambiguationData":[TD([[makeQuery(id+"F16.imprint","IMPRINT",EDGE,{"derivedFrom":sQuery(id+"F16.wireOp",EDGE,"E80")}),-1.0]])]});
            var Q2;
            Q2=makeQuery(id+"F16.imprint","IMPRINT",FACE,{"disambiguationData":[TD([[makeQuery(id+"F16.imprint","IMPRINT",EDGE,{"derivedFrom":sQuery(id+"F16.wireOp",EDGE,"E88.MirrorCS")}),1.0]])]});
            var Q3;
            Q3=makeQuery(id+"F2.opExtrude","CAP_FACE",FACE,{"disambiguationData":[OSD([sQuery(id+"F0.wireOp",EDGE,"E12"),sQuery(id+"F0.wireOp",EDGE,"E13"),sQuery(id+"F0.wireOp",EDGE,"E14"),sQuery(id+"F0.wireOp",EDGE,"E15"),sQuery(id+"F0.wireOp",EDGE,"E17.filletArc"),sQuery(id+"F0.wireOp",EDGE,"E18.filletArc"),sQuery(id+"F0.wireOp",EDGE,"E19.filletArc"),sQuery(id+"F0.wireOp",EDGE,"E20.filletArc"),sQuery(id+"F0.wireOp",EDGE,"E25.0"),sQuery(id+"F0.wireOp",EDGE,"E25.1"),sQuery(id+"F0.wireOp",EDGE,"E25.2"),sQuery(id+"F0.wireOp",EDGE,"E25.3"),sQuery(id+"F0.wireOp",EDGE,"E25.4"),sQuery(id+"F0.wireOp",EDGE,"E25.5"),sQuery(id+"F0.wireOp",EDGE,"E25.6"),sQuery(id+"F0.wireOp",EDGE,"E25.7")])],"isStart":false});
            extrude(context, id + "F17", {"entities" : qUnion([Q0, Q1, Q2]), "endBound" : BoundingType.UP_TO_SURFACE, "endBoundEntityFace" : qUnion([Q3]), "depth" : 25 * mm});
        }
    });
